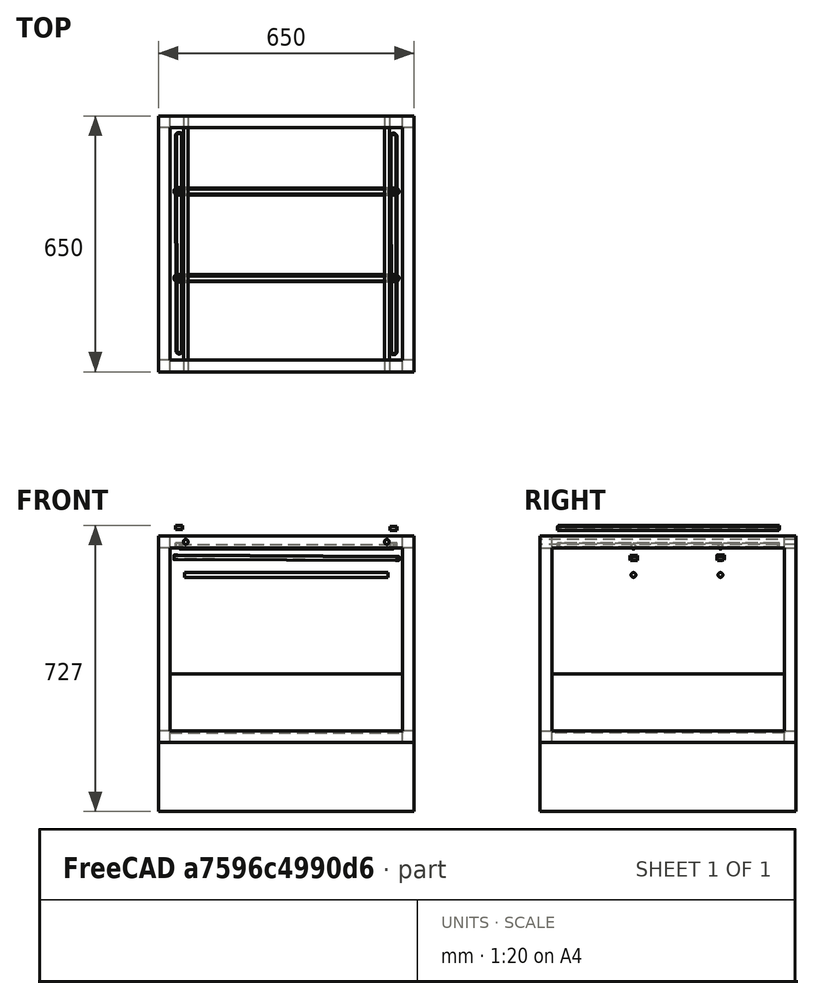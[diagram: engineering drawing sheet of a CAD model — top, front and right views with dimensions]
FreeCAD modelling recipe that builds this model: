
FCSTD DOCUMENT  (FreeCAD 0.16R6698 (Git))
Label: Impresora 3D modelo Modificado
License: All rights reserved
LicenseURL: http://en.wikipedia.org/wiki/All_rights_reserved
objects: Mesh::Feature×80, Part::Box×13, App::DocumentObjectGroup×9, Sketcher::SketchObject×8, Part::Cylinder×6, Part::Sweep×6, Part::MultiFuse×3, PartDesign::Pocket×1
note: 38 computed .brp shape members not serialized (recipe doc carries the construction recipe); baked Part::Feature solids carry a one-line shape summary decoded from their .brp

FEATURE [Part::Box] Box001  label="Vert 1"
  Height = 525
  Length = 30
  Width = 30
FEATURE [Part::Box] Box002  label="Vert 2"
  Height = 525
  Length = 30
  Placement = pos=(620,0,0) rot=(0,0,1;0rad)
  Width = 30
FEATURE [Part::Box] Box003  label="Vert 3"
  Height = 525
  Length = 30
  Placement = pos=(620,620,0) rot=(0,0,1;0rad)
  Width = 30
FEATURE [Part::Box] Box004  label="Vert 4"
  Height = 525
  Length = 30
  Placement = pos=(0,620,0) rot=(0,0,1;0rad)
  Width = 30
FEATURE [Part::Box] Box005  label="Horz 1"
  Height = 30
  Length = 30
  Width = 650
FEATURE [Part::Box] Box006  label="Horz 2"
  Height = 30
  Length = 650
  Width = 30
FEATURE [Part::Box] Box007  label="Horz 3"
  Height = 30
  Length = 650
  Placement = pos=(0,620,0) rot=(0,0,1;0rad)
  Width = 30
FEATURE [Part::Box] Box008  label="Horz 4"
  Height = 30
  Length = 30
  Placement = pos=(620,0,0) rot=(0,0,1;0rad)
  Width = 650
FEATURE [Part::MultiFuse] Fusion  label="Horz Inferior"
  Shapes = -> [Box005,Box006,Box007,Box008]
FEATURE [Part::Box] Box009  label="Horz 005"
  Height = 30
  Length = 30
  Width = 650
FEATURE [Part::Box] Box010  label="Horz 006"
  Height = 30
  Length = 650
  Width = 30
FEATURE [Part::Box] Box011  label="Horz 007"
  Height = 30
  Length = 650
  Placement = pos=(0,620,0) rot=(0,0,1;0rad)
  Width = 30
FEATURE [Part::Box] Box012  label="Horz 008"
  Height = 30
  Length = 30
  Placement = pos=(620,0,0) rot=(0,0,1;0rad)
  Width = 650
FEATURE [Part::MultiFuse] Fusion001  label="Horz Sup"
  Placement = pos=(0,0,495) rot=(0,0,1;0rad)
  Shapes = -> [Box009,Box010,Box011,Box012]
FEATURE [Mesh::Feature] pieza_eje_Y  label="pieza eje Y 1"
  Placement = pos=(616,615,495) rot=(0.707107,-0.707107,0;3.14159rad)
FEATURE [Mesh::Feature] pieza_eje_Y001  label="pieza eje Y 2"
  Placement = pos=(616,34,484) rot=(0,0,1;1.5708rad)
FEATURE [Mesh::Feature] pieza_eje_Y002  label="pieza eje Y 3"
  Placement = pos=(34,616,484) rot=(0,0,-1;1.5708rad)
FEATURE [Mesh::Feature] pieza_eje_Y003  label="pieza eje Y 4"
  Placement = pos=(34,35,484) rot=(0,0,1;0rad)
FEATURE [Part::Cylinder] Cylinder  label="eje y 1"
  Angle = 360
  Height = 650
  Placement = pos=(69.5,650,510) rot=(1,0,0;1.5708rad)
  Radius = 6.1
FEATURE [Part::Cylinder] Cylinder001  label="eje y 2"
  Angle = 360
  Height = 650
  Placement = pos=(580.5,650,510) rot=(1,0,0;1.5708rad)
  Radius = 6.1
FEATURE [Mesh::Feature] rodamiento  label="rodamiento 1"
  Placement = pos=(69,471,510) rot=(0,0,1;1.5708rad)
FEATURE [Mesh::Feature] rodamiento001  label="rodamiento 2"
  Placement = pos=(69,416,510) rot=(0,0,1;1.5708rad)
FEATURE [Mesh::Feature] pieza_eje_X_completa  label="pieza eje X completa"
  Placement = pos=(69,501,510) rot=(0,0,-1;1.5708rad)
FEATURE [Mesh::Feature] rodamiento002  label="rodamiento 003"
  Placement = pos=(580,415,510) rot=(0,0,1;1.5708rad)
FEATURE [Mesh::Feature] rodamiento003  label="rodamiento 004"
  Placement = pos=(580,470,510) rot=(0,0,1;1.5708rad)
FEATURE [Mesh::Feature] pieza_eje_X_completa001  label="pieza eje X completa 2"
  Placement = pos=(580,415,510) rot=(0,0,1;1.5708rad)
FEATURE [Part::Cylinder] Cylinder002  label="eje X 1 - 1"
  Angle = 360
  Height = 517
  Placement = pos=(67,458,426) rot=(0,1,0;1.5708rad)
  Radius = 6
FEATURE [Part::Cylinder] Cylinder003  label="eje X 1 - 2"
  Angle = 360
  Height = 543
  Placement = pos=(54,458,498) rot=(0,1,0;1.5708rad)
  Radius = 6
FEATURE [Mesh::Feature] extrusor  label="extrusor 1"
  Placement = pos=(307,476,442) rot=(0,0,1;0rad)
FEATURE [Mesh::Feature] rodamiento004  label="rodamiento 005"
  Placement = pos=(314,458,498) rot=(0,0,1;0rad)
FEATURE [Mesh::Feature] rodamiento005  label="rodamiento 006"
  Placement = pos=(314,458,426) rot=(0,0,1;0rad)
FEATURE [Mesh::Feature] rodamiento006  label="rodamiento 7"
  Placement = pos=(69,250,510) rot=(0,0,1;1.5708rad)
FEATURE [Mesh::Feature] rodamiento007  label="rodamiento 8"
  Placement = pos=(69,195,510) rot=(0,0,1;1.5708rad)
FEATURE [Mesh::Feature] rodamiento008  label="rodamiento 9"
  Placement = pos=(581,250,510) rot=(0,0,1;1.5708rad)
FEATURE [Mesh::Feature] rodamiento009  label="rodamiento 10"
  Placement = pos=(581,195,510) rot=(0,0,1;1.5708rad)
FEATURE [Part::Cylinder] Cylinder004  label="eje X 2 - 1"
  Angle = 360
  Height = 543
  Placement = pos=(54,237,498) rot=(0,1,0;1.5708rad)
  Radius = 6
FEATURE [Part::Cylinder] Cylinder005  label="eje X 2 - 2"
  Angle = 360
  Height = 517
  Placement = pos=(67,237,426) rot=(0,1,0;1.5708rad)
  Radius = 6
FEATURE [Mesh::Feature] extrusor001  label="extrusor 2"
  Placement = pos=(350,219,441) rot=(0,0,1;3.14159rad)
FEATURE [Mesh::Feature] rodamiento010  label="rodamiento 11"
  Placement = pos=(314,237,498) rot=(0,0,1;0rad)
FEATURE [Mesh::Feature] rodamiento011  label="rodamiento 12"
  Placement = pos=(314,237,426) rot=(0,0,1;0rad)
FEATURE [Mesh::Feature] pieza_eje_Y_adaptada  label="pieza eje Y adaptada 1"
  Placement = pos=(617,616,568) rot=(0.707107,-0.707107,0;3.14159rad)
FEATURE [Mesh::Feature] pieza_eje_Y_adaptada001  label="pieza eje Y adaptada 2"
  Placement = pos=(34,616,568) rot=(1,0,0;3.14159rad)
FEATURE [Mesh::Feature] pieza_eje_Y_adaptada002  label="pieza eje Y adaptada 3"
  Placement = pos=(616,34,568) rot=(0,1,0;3.14159rad)
FEATURE [Mesh::Feature] pieza_eje_Y_adaptada003  label="pieza eje Y adaptada 4"
  Placement = pos=(34,35,568) rot=(0.707093,0.707093,-0.006171;3.12925rad)
FEATURE [Mesh::Feature] Motor_NEMA17  label="NEMA17 1"
  Placement = pos=(53,54,468) rot=(0,0,1;0rad)
FEATURE [Mesh::Feature] Motor_NEMA018  label="NEMA17 2"
  Placement = pos=(598,52,468) rot=(0,0,1;0rad)
FEATURE [Mesh::Feature] Motor_NEMA019  label="NEMA17 3"
  Placement = pos=(328,496,461) rot=(0.57735,-0.57735,-0.57735;4.18879rad)
FEATURE [Mesh::Feature] Motor_NEMA020  label="NEMA17 4"
  Placement = pos=(601,458,433.5) rot=(0,0,1;0rad)
FEATURE [Mesh::Feature] Motor_NEMA021  label="NEMA17 5"
  Placement = pos=(53,54,584) rot=(0,1,0;3.14159rad)
FEATURE [Mesh::Feature] Motor_NEMA022  label="NEMA17 6"
  Placement = pos=(598,52,584) rot=(0,1,0;3.14159rad)
FEATURE [Mesh::Feature] Motor_NEMA023  label="NEMA17 7"
  Placement = pos=(602,237.5,434) rot=(0,0,1;0rad)
FEATURE [Mesh::Feature] Motor_NEMA024  label="NEMA17 8"
  Placement = pos=(327,198.5,463) rot=(1,0,0;1.5708rad)
FEATURE [Mesh::Feature] Pieza_eje_X_MOD  label="Pieza eje X CMP 1 MOD"
  Placement = pos=(69,280,510) rot=(0,0,-1;1.5708rad)
FEATURE [Mesh::Feature] Pieza_eje_X_MOD001  label="Pieza eje X CMP 2 MOD"
  Placement = pos=(581,195,510) rot=(0,0,1;1.5708rad)
FEATURE [Mesh::Feature] Soporte_filamento_DER  label="Soporte filamento DER 1"
  Placement = pos=(91,480,495) rot=(0,0,1;0rad)
FEATURE [Mesh::Feature] Soporte_filamento_IZQ  label="Soporte filamento IZQ 1"
  Placement = pos=(174,480,495) rot=(0,0,1;0rad)
FEATURE [Mesh::Feature] Soporte_filamento_DER001  label="Soporte filamento DER 2"
  Placement = pos=(567,170,495) rot=(0,0,1;3.14159rad)
FEATURE [Mesh::Feature] Soporte_filamento_IZQ001  label="Soporte filamento IZQ 2"
  Placement = pos=(484,170,495) rot=(0,0,1;3.14159rad)
FEATURE [Mesh::Feature] polea1  label="polea type1 1"
  Placement = pos=(53,54,495) rot=(0,-1,0;1.5708rad)
FEATURE [Mesh::Feature] polea1001  label="polea type1 2"
  Placement = pos=(598,52,495) rot=(0,-1,0;1.5708rad)
FEATURE [Mesh::Feature] polea1002  label="polea type1 3"
  Placement = pos=(53,54,558) rot=(0,1,0;1.5708rad)
FEATURE [Mesh::Feature] polea1003  label="polea type1 4"
  Placement = pos=(598,52,556) rot=(0,1,0;1.5708rad)
FEATURE [Mesh::Feature] polea1004  label="polea type 1 5"
  Placement = pos=(602,237,460) rot=(0,-1,0;1.5708rad)
FEATURE [Mesh::Feature] polea1005  label="polea type 1 6"
  Placement = pos=(602,458,460) rot=(0,-1,0;1.5708rad)
FEATURE [Mesh::Feature] polea2  label="polea type2 1"
  Placement = pos=(52.8053,598.93,507.4) rot=(0.087156,0.996195,0;3.14159rad)
FEATURE [Mesh::Feature] polea1006  label="polea type2 2"
  Placement = pos=(52,598,541) rot=(0,0,1;0rad)
FEATURE [Mesh::Feature] polea1007  label="polea type2 3"
  Placement = pos=(597.8,598,496.6) rot=(0,0,1;0rad)
FEATURE [Mesh::Feature] polea1008  label="polea type2 4"
  Placement = pos=(598.8,597,538.6) rot=(0,0,1;0rad)
FEATURE [Mesh::Feature] Soporte_Polea2001  label="Soporte Polea 1"
  Placement = pos=(73.6575,613.53,480) rot=(0,0,1;2.96706rad)
FEATURE [Mesh::Feature] Soporte_Polea2002  label="Soporte Polea 2"
  Placement = pos=(580,580,481) rot=(0,0,1;0rad)
FEATURE [Mesh::Feature] Soporte_Polea2003  label="Soporte Polea 3"
  Placement = pos=(34,616,569) rot=(1,0,0;3.14159rad)
FEATURE [Mesh::Feature] Soporte_Polea2004  label="Soporte Polea 4"
  Placement = pos=(581,616,568) rot=(1,0,0;3.14159rad)
FEATURE [Mesh::Feature] sujeccion_cadena  label="sujeccion cadena 1"
  Placement = pos=(328,217,511) rot=(0,0,1;0rad)
FEATURE [Mesh::Feature] sujeccion_cadena001  label="sujeccion cadena 2"
  Placement = pos=(329,476,512) rot=(0,0,1;3.14159rad)
FEATURE [Mesh::Feature] part_1_extruder  label="part 1 extruder 1"
  Placement = pos=(329,495.7,461) rot=(0,0.707107,0.707107;3.14159rad)
FEATURE [Mesh::Feature] part_1_extruder001  label="part 1 extruder 2"
  Placement = pos=(327,198.7,463) rot=(1,0,0;1.5708rad)
FEATURE [Mesh::Feature] muelle  label="muelle extruder 1"
  Placement = pos=(302.5,513,454) rot=(0,0,1;0rad)
FEATURE [Mesh::Feature] muelle001  label="muelle extruder 2"
  Placement = pos=(331.5,161,456) rot=(0,0,1;0rad)
FEATURE [Mesh::Feature] extruder_drive_gear  label="extruder drive gear 1"
  Placement = pos=(338.88,524,283) rot=(0,0,-1;1.5708rad)
FEATURE [Mesh::Feature] extruder_drive_gear001  label="extruder drive gear 2"
  Placement = pos=(315.88,171,285) rot=(0,0,1;1.5708rad)
FEATURE [Mesh::Feature] fan_40x40  label="fan 40x40 1"
  Placement = pos=(339,508,289) rot=(0,0,-1;1.5708rad)
FEATURE [Mesh::Feature] fan_40x041  label="fan 40x40 2"
  Placement = pos=(339,133,290) rot=(0,0,-1;1.5708rad)
FEATURE [Mesh::Feature] Hotend_main_tube  label="Hotend main tube 1"
  Placement = pos=(332,503,584) rot=(1,0,0;3.14159rad)
FEATURE [Mesh::Feature] Hotend_main_tube001  label="Hotend main tube 2"
  Placement = pos=(324,158,586) rot=(1,0,0;3.14159rad)
FEATURE [Mesh::Feature] nozzle_suport  label="nozzle suport 1"
  Placement = pos=(336,572,383) rot=(0,0,1;0rad)
FEATURE [Mesh::Feature] nozzle_suport001  label="nozzle suport 2"
  Placement = pos=(328,227,383) rot=(0,0,1;0rad)
FEATURE [Mesh::Feature] hotend_nozzle  label="hotend nozzle 1"
  Placement = pos=(332,537,274) rot=(0,0,1;0rad)
FEATURE [Mesh::Feature] hotend_nozzle001  label="hotend nozzle 2"
  Placement = pos=(324,192,274) rot=(0,0,1;0rad)
FEATURE [App::DocumentObjectGroup] Grupo004  label="Extruder axis original"
  Group = -> [fan_40x40,part_1_extruder,nozzle_suport,Hotend_main_tube,extruder_drive_gear,muelle,hotend_nozzle,Motor_NEMA019]
FEATURE [App::DocumentObjectGroup] Grupo005  label="Extruder axis modified"
  Group = -> [hotend_nozzle001,nozzle_suport001,Hotend_main_tube001,fan_40x041,extruder_drive_gear001,muelle001,part_1_extruder001,Motor_NEMA024]
FEATURE [Part::MultiFuse] Fusion002  label="Parte Superior"
  Shapes = -> [Fusion001,Fusion,Box004,Box003,Box002,Box001]
FEATURE [Part::Box] Box013  label="Parte inferior con tapadera"
  Height = 175
  Length = 650
  Placement = pos=(0,0,-175) rot=(0,0,1;0rad)
  Width = 650
FEATURE [Sketcher::SketchObject] Sketch
  ExternalGeometry = -> [Box013]
  Support = -> Box013 [Face6]
  sketch-geometry (9):
    g0: LineSegment StartX=30 StartY=620 StartZ=0 EndX=620 EndY=620 EndZ=0
    g1: LineSegment StartX=620 StartY=620 StartZ=0 EndX=620 EndY=30 EndZ=0
    g2: LineSegment StartX=620 StartY=30 StartZ=0 EndX=30 EndY=30 EndZ=0
    g3: LineSegment StartX=30 StartY=30 StartZ=0 EndX=30 EndY=620 EndZ=0
    g4: LineSegment [constr] StartX=0 StartY=0 StartZ=0 EndX=650 EndY=650 EndZ=0
    g5: LineSegment [constr] StartX=0 StartY=650 StartZ=0 EndX=650 EndY=0 EndZ=0
    g6: LineSegment [constr] StartX=30 StartY=600.993 StartZ=0 EndX=0 EndY=600.993 EndZ=0
    g7: LineSegment [constr] StartX=339.883 StartY=30 StartZ=0 EndX=339.883 EndY=0 EndZ=0
    g8: LineSegment [constr] StartX=132.593 StartY=620 StartZ=0 EndX=132.593 EndY=650 EndZ=0
  constraints (25):
    c: Coincident(g0,g1)
    c: Coincident(g1,g2)
    c: Coincident(g2,g3)
    c: Coincident(g3,g0)
    c: Horizontal(g0)
    c: Horizontal(g2)
    c: Vertical(g1)
    c: Vertical(g3)
    c: Coincident(g4,g-1)
    c: Coincident(g4,g-6)
    c: Coincident(g5,g-6)
    c: Coincident(g5,g-5)
    c: PointOnObject(g1,g5)
    c: PointOnObject(g0,g5)
    c: PointOnObject(g2,g4)
    c: PointOnObject(g6,g3)
    c: Horizontal(g6)
    c: DistanceX(g6,g6) = 30
    c: PointOnObject(g7,g2)
    c: Vertical(g7)
    c: DistanceY(g7,g7) = 30
    c: PointOnObject(g7,g-3)
    c: PointOnObject(g8,g0)
    c: PointOnObject(g8,g-6)
    c: Vertical(g8)
FEATURE [PartDesign::Pocket] Pocket  label="parte inferior con hueco"
  Length = 150
  Placement = pos=(0,0,-175) rot=(0,0,1;0rad)
  Sketch = -> Sketch
  Type = 0
FEATURE [App::DocumentObjectGroup] Grupo007  label="Base"
  Group = -> [Fusion002,Box013,Pocket]
FEATURE [Mesh::Feature] Soporte_Polea2  label="Soporte Polea 5"
  Placement = pos=(30,440.5,448) rot=(0,0,1;0rad)
FEATURE [Mesh::Feature] Soporte_Polea2005  label="Soporte Polea 6"
  Placement = pos=(30.5,219,448) rot=(0,0,1;0rad)
FEATURE [Mesh::Feature] polea2001  label="polea type2 5"
  Placement = pos=(49,458.5,465) rot=(0,0,1;0rad)
FEATURE [Mesh::Feature] polea2002  label="polea type2 6"
  Placement = pos=(49,237.5,465) rot=(0,0,1;0rad)
FEATURE [Sketcher::SketchObject] Sketch001
  sketch-geometry (7):
    g0: ArcOfCircle CenterX=-29.8822 CenterY=7.99999 CenterZ=0 NormalX=0 NormalY=0 NormalZ=1 Radius=8 StartAngle=1.56935 EndAngle=4.71383
    g1: ArcOfCircle CenterX=523.454 CenterY=7.99999 CenterZ=0 NormalX=0 NormalY=0 NormalZ=1 Radius=7.2 StartAngle=4.71383 EndAngle=7.85254
    g2: LineSegment StartX=-29.8707 StartY=16 StartZ=0 EndX=523.464 EndY=15.2 EndZ=0
    g3: Circle [constr] CenterX=523.454 CenterY=7.99999 CenterZ=0 NormalX=0 NormalY=0 NormalZ=1 Radius=7.2
    g4: Circle [constr] CenterX=-29.8822 CenterY=7.99999 CenterZ=0 NormalX=0 NormalY=0 NormalZ=1 Radius=8
    g5: LineSegment [constr] StartX=-29.8822 StartY=7.99999 StartZ=0 EndX=523.454 EndY=7.99999 EndZ=0
    g6: LineSegment StartX=-29.8707 StartY=0 StartZ=0 EndX=523.464 EndY=0.799999 EndZ=0
  constraints (17):
    c: Tangent(g0,g2) = 1.5708
    c: Tangent(g2,g1) = 1.5708
    c: Coincident(g5,g4)
    c: Coincident(g5,g3)
    c: Horizontal(g5)
    c: Coincident(g4,g0)
    c: Coincident(g3,g1)
    c: Radius(g4) = 8
    c: Radius(g3) = 7.2
    c: PointOnObject(g1,g3)
    c: PointOnObject(g0,g4)
    c: DistanceX(g5,g5) = 553.336
    c: PointOnObject(g0,g-1)
    c: Coincident(g6,g1)
    c: Tangent(g6,g3)
    c: Coincident(g6,g0)
    c: Tangent(g6,g4)
FEATURE [Sketcher::SketchObject] Sketch002
  Placement = pos=(0,0,0) rot=(0.57735,0.57735,0.57735;2.0944rad)
  sketch-geometry (4):
    g0: LineSegment StartX=-1.5 StartY=5 StartZ=0 EndX=1.5 EndY=5 EndZ=0
    g1: LineSegment StartX=1.5 StartY=5 StartZ=0 EndX=1.5 EndY=-5 EndZ=0
    g2: LineSegment StartX=1.5 StartY=-5 StartZ=0 EndX=-1.5 EndY=-5 EndZ=0
    g3: LineSegment StartX=-1.5 StartY=-5 StartZ=0 EndX=-1.5 EndY=5 EndZ=0
  constraints (12):
    c: Coincident(g0,g1)
    c: Coincident(g1,g2)
    c: Coincident(g2,g3)
    c: Coincident(g3,g0)
    c: Horizontal(g0)
    c: Horizontal(g2)
    c: Vertical(g1)
    c: Vertical(g3)
    c: DistanceY(g3,g3) = 10
    c: DistanceX(g0,g0) = 3
    c: Symmetric(g0,g0,g-2)
    c: Symmetric(g0,g2,g-1)
FEATURE [Part::Sweep] Sweep  label="correa axis X original"
  Frenet = false
  Placement = pos=(79,450.5,471) rot=(0.957825,0.287341,-0.002508;0.018222rad)
  Sections = -> [Sketch002]
  Solid = true
  Spine = -> Sketch001 [Edge2,Edge1,Edge4,Edge3]
  Transition = 1
FEATURE [Sketcher::SketchObject] Sketch003
  sketch-geometry (7):
    g0: ArcOfCircle CenterX=-29.8822 CenterY=7.99999 CenterZ=0 NormalX=0 NormalY=0 NormalZ=1 Radius=8 StartAngle=1.56935 EndAngle=4.71383
    g1: ArcOfCircle CenterX=523.454 CenterY=7.99999 CenterZ=0 NormalX=0 NormalY=0 NormalZ=1 Radius=7.2 StartAngle=4.71383 EndAngle=7.85254
    g2: LineSegment StartX=-29.8707 StartY=16 StartZ=0 EndX=523.464 EndY=15.2 EndZ=0
    g3: Circle [constr] CenterX=523.454 CenterY=7.99999 CenterZ=0 NormalX=0 NormalY=0 NormalZ=1 Radius=7.2
    g4: Circle [constr] CenterX=-29.8822 CenterY=7.99999 CenterZ=0 NormalX=0 NormalY=0 NormalZ=1 Radius=8
    g5: LineSegment [constr] StartX=-29.8822 StartY=7.99999 StartZ=0 EndX=523.454 EndY=7.99999 EndZ=0
    g6: LineSegment StartX=-29.8707 StartY=0 StartZ=0 EndX=523.464 EndY=0.799999 EndZ=0
  constraints (17):
    c: Tangent(g0,g2) = 1.5708
    c: Tangent(g2,g1) = 1.5708
    c: Coincident(g5,g4)
    c: Coincident(g5,g3)
    c: Horizontal(g5)
    c: Coincident(g4,g0)
    c: Coincident(g3,g1)
    c: Radius(g4) = 8
    c: Radius(g3) = 7.2
    c: PointOnObject(g1,g3)
    c: PointOnObject(g0,g4)
    c: DistanceX(g5,g5) = 553.336
    c: PointOnObject(g0,g-1)
    c: Coincident(g6,g1)
    c: Tangent(g6,g3)
    c: Coincident(g6,g0)
    c: Tangent(g6,g4)
FEATURE [Sketcher::SketchObject] Sketch004
  Placement = pos=(0,0,0) rot=(0.57735,0.57735,0.57735;2.0944rad)
  sketch-geometry (4):
    g0: LineSegment StartX=-1.5 StartY=5 StartZ=0 EndX=1.5 EndY=5 EndZ=0
    g1: LineSegment StartX=1.5 StartY=5 StartZ=0 EndX=1.5 EndY=-5 EndZ=0
    g2: LineSegment StartX=1.5 StartY=-5 StartZ=0 EndX=-1.5 EndY=-5 EndZ=0
    g3: LineSegment StartX=-1.5 StartY=-5 StartZ=0 EndX=-1.5 EndY=5 EndZ=0
  constraints (12):
    c: Coincident(g0,g1)
    c: Coincident(g1,g2)
    c: Coincident(g2,g3)
    c: Coincident(g3,g0)
    c: Horizontal(g0)
    c: Horizontal(g2)
    c: Vertical(g1)
    c: Vertical(g3)
    c: DistanceY(g3,g3) = 10
    c: DistanceX(g0,g0) = 3
    c: Symmetric(g0,g0,g-2)
    c: Symmetric(g0,g2,g-1)
FEATURE [Part::Sweep] Sweep001  label="correa axis X modified"
  Frenet = false
  Placement = pos=(79,230,470) rot=(0.957825,0.287341,-0.002508;0.018222rad)
  Sections = -> [Sketch004]
  Solid = true
  Spine = -> Sketch003 [Edge2,Edge1,Edge4,Edge3]
  Transition = 1
FEATURE [Sketcher::SketchObject] Sketch005
  sketch-geometry (7):
    g0: Circle [constr] CenterX=-7 CenterY=0 CenterZ=0 NormalX=0 NormalY=0 NormalZ=1 Radius=7
    g1: Circle [constr] CenterX=-7.5 CenterY=545.425 CenterZ=0 NormalX=0 NormalY=0 NormalZ=1 Radius=7.5
    g2: LineSegment [constr] StartX=-7.5 StartY=545.425 StartZ=0 EndX=-7 EndY=0 EndZ=0
    g3: ArcOfCircle CenterX=-7 CenterY=0 CenterZ=0 NormalX=0 NormalY=0 NormalZ=1 Radius=7 StartAngle=3.14343 EndAngle=6.28319
    g4: ArcOfCircle CenterX=-7.5 CenterY=545.425 CenterZ=0 NormalX=0 NormalY=0 NormalZ=1 Radius=7.5 StartAngle=0 EndAngle=3.14343
    g5: LineSegment StartX=0 StartY=0 StartZ=0 EndX=0 EndY=545.425 EndZ=0
    g6: LineSegment StartX=-14 StartY=-0.012834 StartZ=0 EndX=-15 EndY=545.411 EndZ=0
  constraints (15):
    c: Radius(g0) = 7
    c: Radius(g1) = 7.5
    c: Coincident(g2,g1)
    c: Coincident(g2,g0)
    c: DistanceY(g2,g2) = 545.425
    c: Tangent(g3,g6) = 1.5708
    c: Tangent(g3,g5) = -1.5708
    c: Tangent(g5,g4) = -1.5708
    c: Tangent(g6,g4) = 1.5708
    c: Vertical(g5)
    c: Coincident(g4,g1)
    c: Coincident(g3,g0)
    c: Tangent(g5,g0)
    c: Tangent(g5,g1)
    c: Coincident(g-1,g3)
FEATURE [Sketcher::SketchObject] Sketch006
  Placement = pos=(0,0,0) rot=(1,0,0;1.5708rad)
  sketch-geometry (4):
    g0: LineSegment StartX=-1.5 StartY=5 StartZ=0 EndX=1.5 EndY=5 EndZ=0
    g1: LineSegment StartX=1.5 StartY=5 StartZ=0 EndX=1.5 EndY=-5 EndZ=0
    g2: LineSegment StartX=1.5 StartY=-5 StartZ=0 EndX=-1.5 EndY=-5 EndZ=0
    g3: LineSegment StartX=-1.5 StartY=-5 StartZ=0 EndX=-1.5 EndY=5 EndZ=0
  constraints (12):
    c: Coincident(g0,g1)
    c: Coincident(g1,g2)
    c: Coincident(g2,g3)
    c: Coincident(g3,g0)
    c: Horizontal(g0)
    c: Horizontal(g2)
    c: Vertical(g1)
    c: Vertical(g3)
    c: DistanceY(g1,g1) = 10
    c: DistanceX(g2,g2) = 3
    c: Symmetric(g0,g0,g-2)
    c: Symmetric(g0,g2,g-1)
FEATURE [Part::Sweep] Sweep002  label="Correa 1 Axis Y original"
  Frenet = false
  Placement = pos=(60,54,502) rot=(0,0,1;0rad)
  Sections = -> [Sketch006]
  Solid = true
  Spine = -> Sketch005 [Edge4,Edge1,Edge2,Edge3]
  Transition = 1
FEATURE [Sketcher::SketchObject] Sketch007
  sketch-geometry (7):
    g0: Circle [constr] CenterX=-7 CenterY=0 CenterZ=0 NormalX=0 NormalY=0 NormalZ=1 Radius=7
    g1: Circle [constr] CenterX=-7.5 CenterY=545.425 CenterZ=0 NormalX=0 NormalY=0 NormalZ=1 Radius=7.5
    g2: LineSegment [constr] StartX=-7.5 StartY=545.425 StartZ=0 EndX=-7 EndY=0 EndZ=0
    g3: ArcOfCircle CenterX=-7 CenterY=0 CenterZ=0 NormalX=0 NormalY=0 NormalZ=1 Radius=7 StartAngle=3.14343 EndAngle=6.28319
    g4: ArcOfCircle CenterX=-7.5 CenterY=545.425 CenterZ=0 NormalX=0 NormalY=0 NormalZ=1 Radius=7.5 StartAngle=0 EndAngle=3.14343
    g5: LineSegment StartX=0 StartY=0 StartZ=0 EndX=0 EndY=545.425 EndZ=0
    g6: LineSegment StartX=-14 StartY=-0.012834 StartZ=0 EndX=-15 EndY=545.411 EndZ=0
  constraints (15):
    c: Radius(g0) = 7
    c: Radius(g1) = 7.5
    c: Coincident(g2,g1)
    c: Coincident(g2,g0)
    c: DistanceY(g2,g2) = 545.425
    c: Tangent(g3,g6) = 1.5708
    c: Tangent(g3,g5) = -1.5708
    c: Tangent(g5,g4) = -1.5708
    c: Tangent(g6,g4) = 1.5708
    c: Vertical(g5)
    c: Coincident(g4,g1)
    c: Coincident(g3,g0)
    c: Tangent(g5,g0)
    c: Tangent(g5,g1)
    c: Coincident(g-1,g3)
FEATURE [App::DocumentObjectGroup] Grupo008  label="Aux"
  Group = -> [Sketch003,Sketch001,Sketch007,Sketch005]
FEATURE [Part::Sweep] Sweep003  label="Correa 2 Axis Y original"
  Frenet = false
  Placement = pos=(605,52,502) rot=(0,0,1;0rad)
  Sections = -> [Sketch006]
  Solid = true
  Spine = -> Sketch005 [Edge4,Edge1,Edge2,Edge3]
  Transition = 1
FEATURE [App::DocumentObjectGroup] Grupo002  label="Axis Y original"
  Group = -> [Motor_NEMA018,Motor_NEMA17,pieza_eje_Y,pieza_eje_Y001,pieza_eje_Y002,pieza_eje_Y003,polea1007,polea2,polea1001,polea1,Cylinder,Cylinder001,Soporte_Polea2002,Soporte_Polea2001,Sweep002,Sweep003]
FEATURE [Part::Sweep] Sweep004  label="Correa 1 Axis Y modified"
  Frenet = false
  Placement = pos=(60,54,547) rot=(0,0,1;0rad)
  Sections = -> [Sketch006]
  Solid = true
  Spine = -> Sketch005 [Edge4,Edge1,Edge2,Edge3]
  Transition = 1
FEATURE [Part::Sweep] Sweep005  label="Correa 2 Axis Y modified"
  Frenet = false
  Placement = pos=(605,52,544) rot=(0,0,1;0rad)
  Sections = -> [Sketch006]
  Solid = true
  Spine = -> Sketch005 [Edge4,Edge1,Edge2,Edge3]
  Transition = 1
FEATURE [App::DocumentObjectGroup] Grupo003  label="Axis Y modified"
  Group = -> [pieza_eje_Y_adaptada,pieza_eje_Y_adaptada001,pieza_eje_Y_adaptada002,pieza_eje_Y_adaptada003,Motor_NEMA022,Motor_NEMA021,polea1002,polea1003,polea1008,polea1006,Soporte_Polea2003,Soporte_Polea2004,Sweep004,Sweep005]
FEATURE [Mesh::Feature] agarre_polea_extrusor  label="agarre polea extrusor original"
  Placement = pos=(351.3,456,442) rot=(0,0,1;3.14159rad)
FEATURE [App::DocumentObjectGroup] Grupo  label="Axis X original"
  Group = -> [sujeccion_cadena001,pieza_eje_X_completa,pieza_eje_X_completa001,extrusor,polea1005,Motor_NEMA020,rodamiento005,rodamiento004,Cylinder002,rodamiento003,rodamiento002,rodamiento001,rodamiento,Cylinder003,Soporte_Polea2,polea2001,Sweep,agarre_polea_extrusor]
FEATURE [Mesh::Feature] agarre_polea_extrusor001  label="agarre polea extrusor modified"
  Placement = pos=(305.8,239,441) rot=(0,0,1;0rad)
FEATURE [App::DocumentObjectGroup] Grupo001  label="Axis X Modified"
  Group = -> [sujeccion_cadena,Pieza_eje_X_MOD001,Pieza_eje_X_MOD,rodamiento011,rodamiento010,extrusor001,Cylinder004,Cylinder005,rodamiento009,rodamiento008,rodamiento007,rodamiento006,Motor_NEMA023,polea1004,Soporte_Polea2005,polea2002,Sweep001,agarre_polea_extrusor001]
FEATURE [Mesh::Feature] end_stop  label="end-stop 1"
  Placement = pos=(563,448,509) rot=(0.57735,0.57735,0.57735;2.0944rad)
FEATURE [Mesh::Feature] end_stop001  label="end-stop 2"
  Placement = pos=(564,211,540) rot=(0.57735,0.57735,0.57735;2.0944rad)
FEATURE [Mesh::Feature] end_stop002  label="end-stop 3"
  Placement = pos=(68,262,465) rot=(1,0,0;1.5708rad)
FEATURE [Mesh::Feature] end_stop003  label="end-stop 004"
  Placement = pos=(619,52,416) rot=(0.57735,-0.57735,0.57735;4.18879rad)
FEATURE [Mesh::Feature] end_stop_botton  label="end-stop-activator 1"
  Placement = pos=(339,476,515) rot=(0,0,-1;1.5708rad)
FEATURE [Mesh::Feature] end_stop_botton001  label="end-stop-activator 2"
  Placement = pos=(339,228,515) rot=(0,0,-1;1.5708rad)
FEATURE [App::DocumentObjectGroup] Grupo006  label="Complements"
  Group = -> [Soporte_filamento_DER,Soporte_filamento_IZQ,Soporte_filamento_DER001,Soporte_filamento_IZQ001,end_stop,end_stop001,end_stop002,end_stop003,end_stop_botton,end_stop_botton001]
